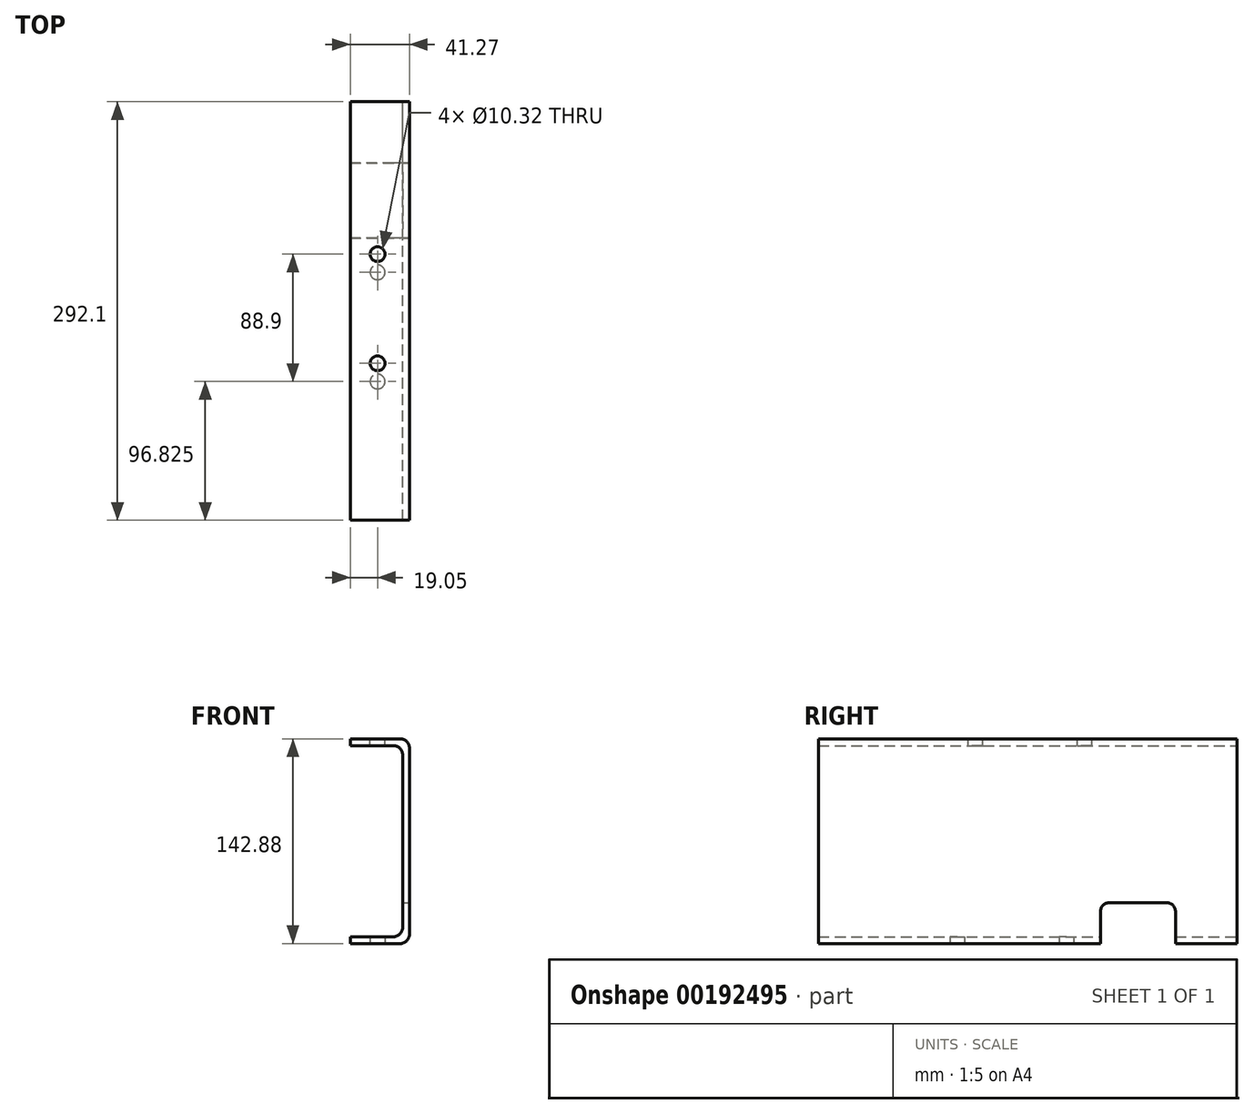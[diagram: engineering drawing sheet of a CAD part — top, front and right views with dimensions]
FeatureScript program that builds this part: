
annotation { "Feature Type Name" : "Feature", "Feature Type Description" : "" }
export const myFeature = defineFeature(function(context is Context, id is Id, definition is map)
    precondition{}
    {
        {
            var Q0;
            Q0=qCreatedBy(makeId("Front.planeOp"),FACE);
            var sketch = newSketch(context, id + "F0", { "sketchPlane" : qUnion([Q0])});
            skLineSegment(sketch, "E0.bottom", {"start": v(0, 0) * mm, "end": v(34.93, 0) * mm});
            skLineSegment(sketch, "E0.top", {"start": v(0, 142.88) * mm, "end": v(34.92, 142.88) * mm});
            skLineSegment(sketch, "E0.left", {"start": v(0, 0) * mm, "end": v(0, 4.76) * mm});
            skLineSegment(sketch, "E0.right", {"start": v(41.28, 6.35) * mm, "end": v(41.27, 136.53) * mm});
            skLineSegment(sketch, "E1.0", {"start": v(0, 138.11) * mm, "end": v(30.16, 138.11) * mm});
            skLineSegment(sketch, "E2.0", {"start": v(36.51, 11.11) * mm, "end": v(36.51, 131.76) * mm});
            skLineSegment(sketch, "E2.1", {"start": v(0, 4.76) * mm, "end": v(30.16, 4.76) * mm});
            skLineSegment(sketch, "E3.trimOffspring", {"start": v(0, 138.11) * mm, "end": v(0, 142.88) * mm});
            skPoint(sketch, "E4.visualSharp", {"position": v(36.51, 138.11) * mm});
            skArc(sketch, "E4.filletArc", {"start": v(36.51, 131.76) * mm, "mid": v(34.65, 136.25) * mm, "end": v(30.16, 138.11) * mm});
            skPoint(sketch, "E5.visualSharp", {"position": v(36.51, 4.76) * mm});
            skArc(sketch, "E5.filletArc", {"start": v(30.16, 4.76) * mm, "mid": v(34.65, 6.62) * mm, "end": v(36.51, 11.11) * mm});
            skPoint(sketch, "E6.visualSharp", {"position": v(41.27, 142.88) * mm});
            skArc(sketch, "E6.filletArc", {"start": v(41.27, 136.53) * mm, "mid": v(39.42, 141.02) * mm, "end": v(34.92, 142.87) * mm});
            skPoint(sketch, "E7.visualSharp", {"position": v(41.28, 0) * mm});
            skArc(sketch, "E7.filletArc", {"start": v(34.93, 0) * mm, "mid": v(39.42, 1.86) * mm, "end": v(41.28, 6.35) * mm});
            skSolve(sketch);
        }
        {
            var Q0;
            Q0 = qSketchRegion(id + "F0", true);
            extrude(context, id + "F1", {"entities" : qUnion([Q0]), "depth" : 292.1 * mm});
        }
        {
            var Q0;
            Q0=makeQuery(id+"F1.opExtrude","SWEPT_FACE",FACE,{"disambiguationData":[OSD([sQuery(id+"F0.wireOp",EDGE,"E0.right")])]});
            var sketch = newSketch(context, id + "F2", { "sketchPlane" : qUnion([Q0])});
            skLineSegment(sketch, "E8.bottom", {"start": v(-95.25, 0) * mm, "end": v(-42.86, 0) * mm});
            skLineSegment(sketch, "E8.top", {"start": v(-88.9, 28.58) * mm, "end": v(-49.21, 28.58) * mm});
            skLineSegment(sketch, "E8.left", {"start": v(-95.25, 0) * mm, "end": v(-95.25, 22.22) * mm});
            skLineSegment(sketch, "E8.right", {"start": v(-42.86, 0) * mm, "end": v(-42.86, 22.23) * mm});
            skPoint(sketch, "E9.visualSharp", {"position": v(-42.86, 28.57) * mm});
            skArc(sketch, "E9.filletArc", {"start": v(-42.86, 22.23) * mm, "mid": v(-44.72, 26.72) * mm, "end": v(-49.21, 28.57) * mm});
            skPoint(sketch, "E10.visualSharp", {"position": v(-95.25, 28.57) * mm});
            skArc(sketch, "E10.filletArc", {"start": v(-88.9, 28.57) * mm, "mid": v(-93.4, 26.72) * mm, "end": v(-95.25, 22.22) * mm});
            skSolve(sketch);
        }
        {
            var Q0;
            Q0 = qSketchRegion(id + "F2", true);
            extrude(context, id + "F3", {"entities" : qUnion([Q0]), "operationType" : NewBodyOperationType.REMOVE, "endBound" : BoundingType.THROUGH_ALL, "oppositeDirection" : true, "depth" : 25.4 * mm});
        }
        {
            var Q0;
            Q0=makeQuery(id+"F1.opExtrude","SWEPT_FACE",FACE,{"disambiguationData":[OSD([sQuery(id+"F0.wireOp",EDGE,"E0.top")])]});
            var sketch = newSketch(context, id + "F4", { "sketchPlane" : qUnion([Q0])});
            skCircle(sketch, "E11", {"center": v(19.05, -106.38) * mm, "radius": 5.16 * mm});
            skCircle(sketch, "E12.0.1.0", {"center": v(19.05, -182.58) * mm, "radius": 5.16 * mm});
            skLineSegment(sketch, "E12.direction1", {"start": v(19.05, -106.38) * mm, "end": v(44.45, -106.38) * mm, "construction": true});
            skLineSegment(sketch, "E12.direction2", {"start": v(19.05, -106.38) * mm, "end": v(19.05, -182.58) * mm, "construction": true});
            skSolve(sketch);
        }
        {
            var Q0;
            Q0 = qSketchRegion(id + "F4", true);
            extrude(context, id + "F5", {"entities" : qUnion([Q0]), "operationType" : NewBodyOperationType.REMOVE, "endBound" : BoundingType.UP_TO_NEXT, "oppositeDirection" : true, "depth" : 25.4 * mm});
        }
        {
            var Q0;
            {var subQ2=sQuery(id+"F0.wireOp",EDGE,"E0.bottom");Q0=makeQuery(id+"F3.boolean.opBoolean","SPLIT",FACE,{"disambiguationData":[TD([makeQuery(id+"F3.opExtrude","SWEPT_FACE",FACE,{"disambiguationData":[OSD([sQuery(id+"F2.wireOp",EDGE,"E8.right")])]})])],"derivedFrom":makeQuery(id+"F1.opExtrude","SWEPT_FACE",FACE,{"disambiguationData":[OSD([subQ2])]})});}
            var sketch = newSketch(context, id + "F6", { "sketchPlane" : qUnion([Q0])});
            skCircle(sketch, "E13", {"center": v(19.05, 119.08) * mm, "radius": 5.16 * mm});
            skCircle(sketch, "E14.0.1.0", {"center": v(19.05, 195.28) * mm, "radius": 5.16 * mm});
            skLineSegment(sketch, "E14.direction1", {"start": v(19.05, 119.08) * mm, "end": v(44.45, 119.08) * mm, "construction": true});
            skLineSegment(sketch, "E14.direction2", {"start": v(19.05, 119.08) * mm, "end": v(19.05, 195.28) * mm, "construction": true});
            skSolve(sketch);
        }
        {
            var Q0;
            Q0 = qSketchRegion(id + "F6", true);
            extrude(context, id + "F7", {"entities" : qUnion([Q0]), "operationType" : NewBodyOperationType.REMOVE, "endBound" : BoundingType.UP_TO_NEXT, "oppositeDirection" : true, "depth" : 25.4 * mm});
        }
    });
